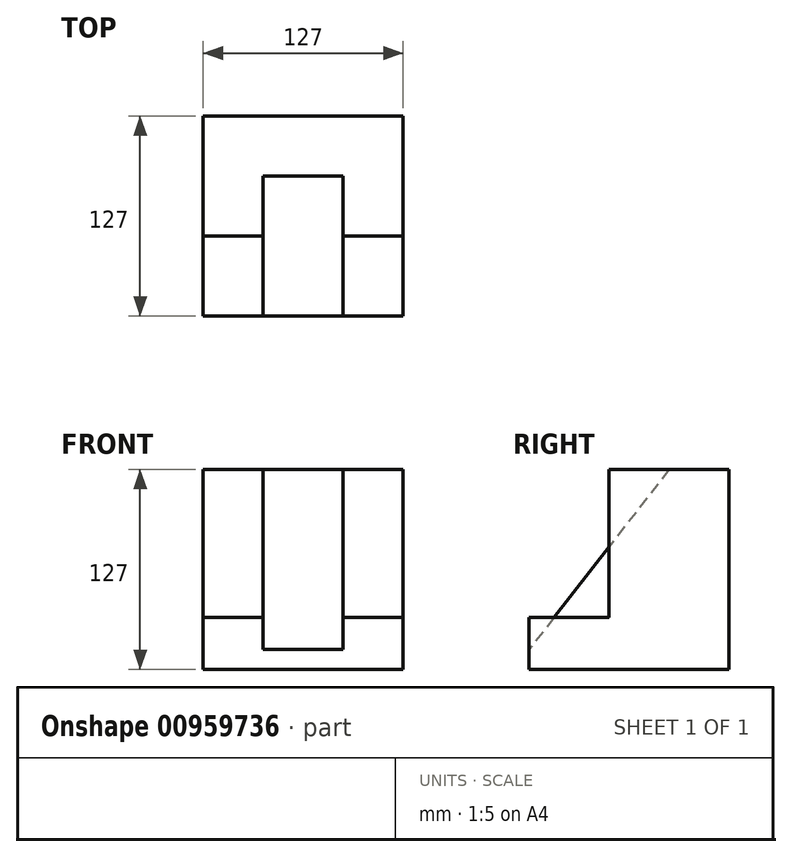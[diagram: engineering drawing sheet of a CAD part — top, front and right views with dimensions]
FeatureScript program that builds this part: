
annotation { "Feature Type Name" : "Feature", "Feature Type Description" : "" }
export const myFeature = defineFeature(function(context is Context, id is Id, definition is map)
    precondition{}
    {
        {
            var Q0;
            Q0=qCreatedBy(makeId("Top.planeOp"),FACE);
            var sketch = newSketch(context, id + "F0", { "sketchPlane" : qUnion([Q0])});
            skLineSegment(sketch, "E0.bottom", {"start": v(-63.5, 63.5) * mm, "end": v(63.5, 63.5) * mm});
            skLineSegment(sketch, "E0.top", {"start": v(-63.5, -63.5) * mm, "end": v(63.5, -63.5) * mm});
            skLineSegment(sketch, "E0.left", {"start": v(-63.5, 63.5) * mm, "end": v(-63.5, -63.5) * mm});
            skLineSegment(sketch, "E0.right", {"start": v(63.5, 63.5) * mm, "end": v(63.5, -63.5) * mm});
            skPoint(sketch, "E0.middle", {"position": v(0, 0) * mm});
            skSolve(sketch);
        }
        {
            var Q0;
            Q0=makeQuery(id+"F0.imprint","IMPRINT",FACE,{"disambiguationData":[TD([[makeQuery(id+"F0.imprint","IMPRINT",EDGE,{"derivedFrom":sQuery(id+"F0.wireOp",EDGE,"E0.bottom")}),-1.0]])]});
            extrude(context, id + "F1", {"entities" : qUnion([Q0]), "depth" : 127 * mm, "offsetDistance" : 25.4 * mm});
        }
        {
            var Q0;
            Q0=makeQuery(id+"F1.opExtrude","CAP_FACE",FACE,{"disambiguationData":[OSD([sQuery(id+"F0.wireOp",EDGE,"E0.bottom"),sQuery(id+"F0.wireOp",EDGE,"E0.top"),sQuery(id+"F0.wireOp",EDGE,"E0.left"),sQuery(id+"F0.wireOp",EDGE,"E0.right")])],"isStart":false});
            var sketch = newSketch(context, id + "F2", { "sketchPlane" : qUnion([Q0])});
            skLineSegment(sketch, "E1.bottom", {"start": v(-63.5, 63.5) * mm, "end": v(63.5, 63.5) * mm});
            skLineSegment(sketch, "E1.top", {"start": v(-63.5, 25.4) * mm, "end": v(63.5, 25.4) * mm});
            skLineSegment(sketch, "E1.left", {"start": v(-63.5, 63.5) * mm, "end": v(-63.5, 25.4) * mm});
            skLineSegment(sketch, "E1.right", {"start": v(63.5, 63.5) * mm, "end": v(63.5, 25.4) * mm});
            skSolve(sketch);
        }
        {
            var Q0;
            Q0=makeQuery(id+"F1.opExtrude","SWEPT_FACE",FACE,{"disambiguationData":[OSD([sQuery(id+"F0.wireOp",EDGE,"E0.right")])]});
            var sketch = newSketch(context, id + "F3", { "sketchPlane" : qUnion([Q0])});
            skLineSegment(sketch, "E2.bottom", {"start": v(-63.5, 0) * mm, "end": v(63.5, 0) * mm});
            skLineSegment(sketch, "E2.top", {"start": v(-63.5, 12.7) * mm, "end": v(63.5, 12.7) * mm});
            skLineSegment(sketch, "E2.left", {"start": v(-63.5, 0) * mm, "end": v(-63.5, 12.7) * mm});
            skLineSegment(sketch, "E2.right", {"start": v(63.5, 0) * mm, "end": v(63.5, 12.7) * mm});
            skLineSegment(sketch, "E3", {"start": v(25.4, 127) * mm, "end": v(-63.5, 12.7) * mm});
            skSolve(sketch);
        }
        {
            var Q0;
            {var subQ0=sQuery(id+"F3.wireOp",EDGE,"E3");Q0=makeQuery(id+"F3.imprint","IMPRINT",FACE,{"disambiguationData":[TD([[makeQuery(id+"F3.imprint","IMPRINT",EDGE,{"derivedFrom":subQ0}),-1.0]])]});}
            extrude(context, id + "F4", {"entities" : qUnion([Q0]), "operationType" : NewBodyOperationType.REMOVE, "oppositeDirection" : true, "depth" : 88.9 * mm, "offsetDistance" : 25.4 * mm});
        }
        {
            var Q0;
            Q0=makeQuery(id+"F2.imprint","IMPRINT",FACE,{"disambiguationData":[TD([[makeQuery(id+"F2.imprint","IMPRINT",EDGE,{"derivedFrom":sQuery(id+"F2.wireOp",EDGE,"E1.bottom")}),-1.0]])]});
            var sketch = newSketch(context, id + "F5", { "sketchPlane" : qUnion([Q0])});
            skLineSegment(sketch, "E4.bottom", {"start": v(63.5, 63.5) * mm, "end": v(25.4, 63.5) * mm});
            skLineSegment(sketch, "E4.top", {"start": v(63.5, -63.5) * mm, "end": v(25.4, -63.5) * mm});
            skLineSegment(sketch, "E4.left", {"start": v(63.5, 63.5) * mm, "end": v(63.5, -63.5) * mm});
            skLineSegment(sketch, "E4.right", {"start": v(25.4, 63.5) * mm, "end": v(25.4, -63.5) * mm});
            skSolve(sketch);
        }
        {
            var Q0;
            {var subQ0=sQuery(id+"F5.wireOp",EDGE,"E4.top");Q0=makeQuery(id+"F5.imprint","IMPRINT",FACE,{"disambiguationData":[TD([[makeQuery(id+"F5.imprint","IMPRINT",EDGE,{"derivedFrom":subQ0}),-1.0]])]});}
            extrude(context, id + "F6", {"entities" : qUnion([Q0]), "operationType" : NewBodyOperationType.ADD, "oppositeDirection" : true, "depth" : 127 * mm, "offsetDistance" : 25.4 * mm});
        }
        {
            var Q0;
            {var subQ0=sQuery(id+"F2.wireOp",EDGE,"E1.top");Q0=makeQuery(id+"F2.imprint","IMPRINT",FACE,{"disambiguationData":[TD([[makeQuery(id+"F2.imprint","IMPRINT",EDGE,{"derivedFrom":subQ0}),-1.0]])]});}
            var sketch = newSketch(context, id + "F7", { "sketchPlane" : qUnion([Q0])});
            skLineSegment(sketch, "E5.bottom", {"start": v(63.5, -63.59) * mm, "end": v(25.4, -63.59) * mm});
            skLineSegment(sketch, "E5.top", {"start": v(63.5, -12.79) * mm, "end": v(25.4, -12.79) * mm});
            skLineSegment(sketch, "E5.left", {"start": v(63.5, -63.59) * mm, "end": v(63.5, -12.79) * mm});
            skLineSegment(sketch, "E5.right", {"start": v(25.4, -63.59) * mm, "end": v(25.4, -12.79) * mm});
            skLineSegment(sketch, "E6.bottom", {"start": v(-25.4, -63.36) * mm, "end": v(-63.5, -63.36) * mm});
            skLineSegment(sketch, "E6.top", {"start": v(-25.4, -12.56) * mm, "end": v(-63.5, -12.56) * mm});
            skLineSegment(sketch, "E6.left", {"start": v(-25.4, -63.36) * mm, "end": v(-25.4, -12.56) * mm});
            skLineSegment(sketch, "E6.right", {"start": v(-63.5, -63.36) * mm, "end": v(-63.5, -12.56) * mm});
            skSolve(sketch);
        }
        {
            var Q0;
            {var subQ0=sQuery(id+"F7.wireOp",EDGE,"E5.top");Q0=makeQuery(id+"F7.imprint","IMPRINT",FACE,{"disambiguationData":[TD([[makeQuery(id+"F7.imprint","IMPRINT",EDGE,{"derivedFrom":subQ0}),1.0]])]});}
            var Q1;
            Q1=makeQuery(id+"F7.imprint","IMPRINT",FACE,{"disambiguationData":[TD([[makeQuery(id+"F7.imprint","IMPRINT",EDGE,{"derivedFrom":sQuery(id+"F7.wireOp",EDGE,"E6.bottom")}),-1.0]])]});
            extrude(context, id + "F8", {"entities" : qUnion([Q0, Q1]), "operationType" : NewBodyOperationType.REMOVE, "oppositeDirection" : true, "depth" : 93.98 * mm, "offsetDistance" : 25.4 * mm});
        }
        {
            var Q0;
            Q0=makeQuery(id+"F6.boolean.opBoolean","MERGE",FACE,{"derivedFrom":[makeQuery(id+"F1.opExtrude","SWEPT_FACE",FACE,{"disambiguationData":[OSD([sQuery(id+"F0.wireOp",EDGE,"E0.top")])]}),makeQuery(id+"F6.opExtrude","SWEPT_FACE",FACE,{"disambiguationData":[OSD([sQuery(id+"F5.wireOp",EDGE,"E4.top")])]})]});
            var sketch = newSketch(context, id + "F9", { "sketchPlane" : qUnion([Q0])});
            skLineSegment(sketch, "E7.bottom", {"start": v(-63.5, 127) * mm, "end": v(-25.4, 127) * mm});
            skLineSegment(sketch, "E7.top", {"start": v(-63.5, 33.02) * mm, "end": v(-25.4, 33.02) * mm});
            skLineSegment(sketch, "E7.left", {"start": v(-63.5, 127) * mm, "end": v(-63.5, 33.02) * mm});
            skLineSegment(sketch, "E7.right", {"start": v(-25.4, 127) * mm, "end": v(-25.4, 33.02) * mm});
            skSolve(sketch);
        }
        {
            var Q0;
            Q0=makeQuery(id+"F9.imprint","IMPRINT",FACE,{"disambiguationData":[TD([[makeQuery(id+"F9.imprint","IMPRINT",EDGE,{"derivedFrom":sQuery(id+"F9.wireOp",EDGE,"E7.bottom")}),-1.0]])]});
            extrude(context, id + "F10", {"entities" : qUnion([Q0]), "operationType" : NewBodyOperationType.REMOVE, "oppositeDirection" : true, "depth" : 12.7 * mm, "offsetDistance" : 25.4 * mm});
        }
    });
